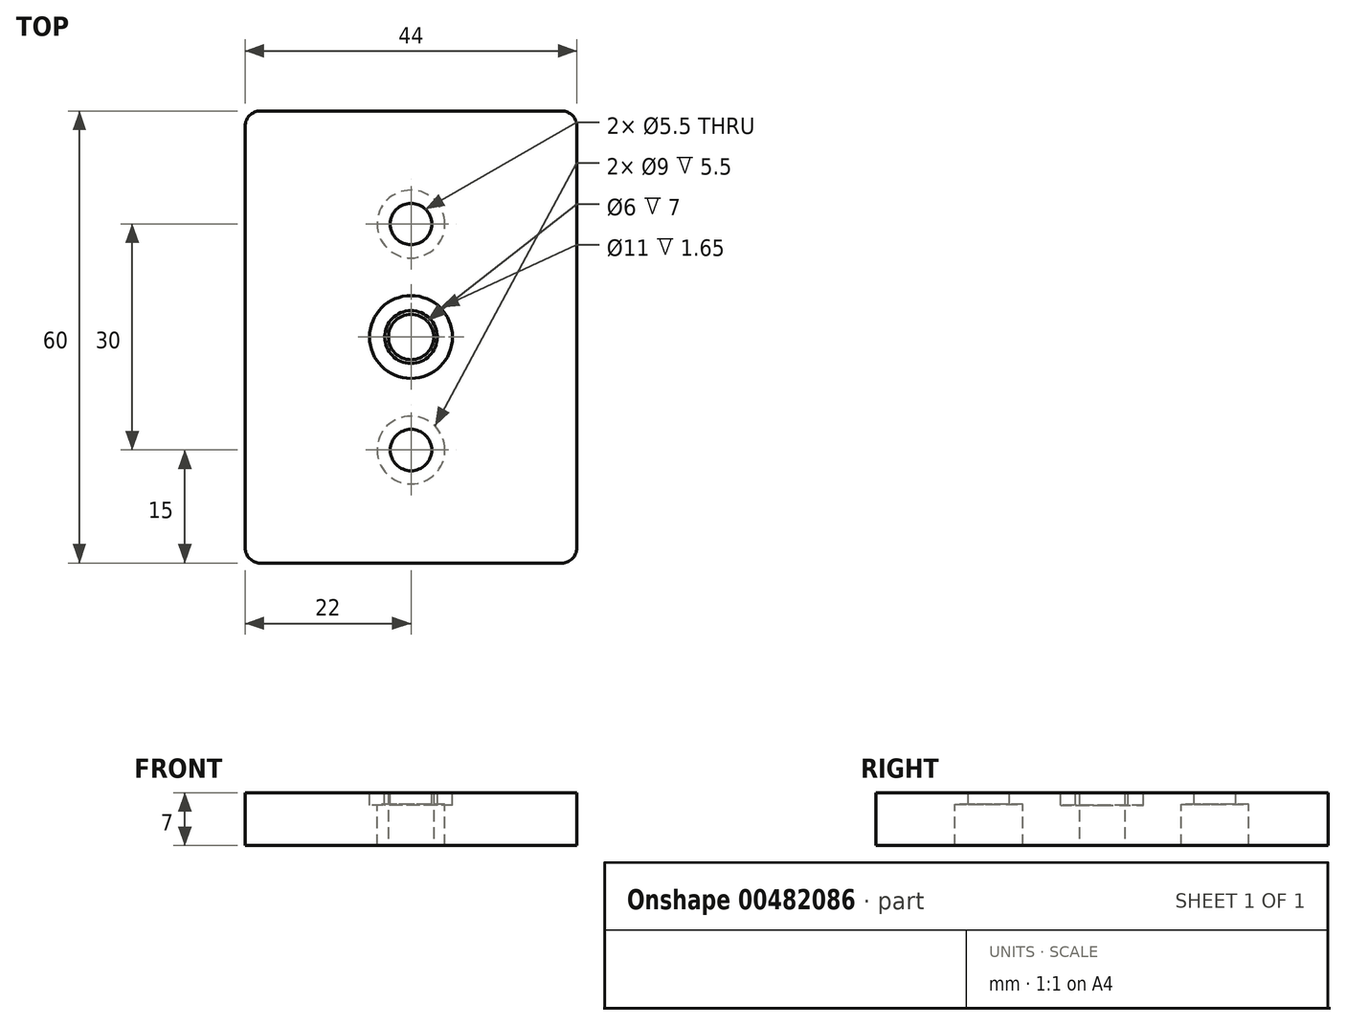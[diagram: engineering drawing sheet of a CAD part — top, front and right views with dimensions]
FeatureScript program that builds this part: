
annotation { "Feature Type Name" : "Feature", "Feature Type Description" : "" }
export const myFeature = defineFeature(function(context is Context, id is Id, definition is map)
    precondition{}
    {
        {
            var Q0;
            Q0=qCreatedBy(makeId("Top.planeOp"),FACE);
            var sketch = newSketch(context, id + "F0", { "sketchPlane" : qUnion([Q0])});
            skLineSegment(sketch, "E0.bottom", {"start": v(-22, 30) * mm, "end": v(22, 30) * mm});
            skLineSegment(sketch, "E0.top", {"start": v(-22, -30) * mm, "end": v(22, -30) * mm});
            skLineSegment(sketch, "E0.left", {"start": v(-22, 30) * mm, "end": v(-22, -30) * mm});
            skLineSegment(sketch, "E0.right", {"start": v(22, 30) * mm, "end": v(22, -30) * mm});
            skSolve(sketch);
        }
        {
            var Q0;
            Q0=makeQuery(id+"F0.imprint","IMPRINT",FACE,{"disambiguationData":[TD([[makeQuery(id+"F0.imprint","IMPRINT",EDGE,{"derivedFrom":sQuery(id+"F0.wireOp",EDGE,"E0.bottom")}),-1.0]])]});
            extrude(context, id + "F1", {"entities" : qUnion([Q0]), "depth" : 7 * mm, "offsetDistance" : 25 * mm});
        }
        {
            var Q0;
            Q0=makeQuery(id+"F1.opExtrude","SWEPT_EDGE",EDGE,{"disambiguationData":[OSD([sQuery(id+"F0.wireOp",EDGE,"E0.top"),sQuery(id+"F0.wireOp",EDGE,"E0.left")])]});
            var Q1;
            Q1=makeQuery(id+"F1.opExtrude","SWEPT_EDGE",EDGE,{"disambiguationData":[OSD([sQuery(id+"F0.wireOp",EDGE,"E0.top"),sQuery(id+"F0.wireOp",EDGE,"E0.right")])]});
            var Q2;
            Q2=makeQuery(id+"F1.opExtrude","SWEPT_EDGE",EDGE,{"disambiguationData":[OSD([sQuery(id+"F0.wireOp",EDGE,"E0.bottom"),sQuery(id+"F0.wireOp",EDGE,"E0.right")])]});
            var Q3;
            Q3=makeQuery(id+"F1.opExtrude","SWEPT_EDGE",EDGE,{"disambiguationData":[OSD([sQuery(id+"F0.wireOp",EDGE,"E0.bottom"),sQuery(id+"F0.wireOp",EDGE,"E0.left")])]});
            fillet(context, id + "F2", {"entities" : qUnion([Q0, Q1, Q2, Q3]), "radius" : 2 * mm, "tangentPropagation" : true, "allowEdgeOverflow" : false});
        }
        {
            var Q0;
            Q0=makeQuery(id+"F1.opExtrude","CAP_FACE",FACE,{"disambiguationData":[OSD([sQuery(id+"F0.wireOp",EDGE,"E0.bottom"),sQuery(id+"F0.wireOp",EDGE,"E0.top"),sQuery(id+"F0.wireOp",EDGE,"E0.left"),sQuery(id+"F0.wireOp",EDGE,"E0.right")])],"isStart":true});
            var sketch = newSketch(context, id + "F3", { "sketchPlane" : qUnion([Q0])});
            skCircle(sketch, "E1", {"center": v(0, 0) * mm, "radius": 3 * mm});
            skPoint(sketch, "E2", {"position": v(0, -15) * mm});
            skPoint(sketch, "E3", {"position": v(0, 15) * mm});
            skSolve(sketch);
        }
        {
            var Q0;
            Q0=makeQuery(id+"F3.imprint","IMPRINT",FACE,{"disambiguationData":[TD([[makeQuery(id+"F3.imprint","IMPRINT",EDGE,{"derivedFrom":sQuery(id+"F3.wireOp",EDGE,"E1")}),1.0]])]});
            extrude(context, id + "F4", {"entities" : qUnion([Q0]), "operationType" : NewBodyOperationType.REMOVE, "endBound" : BoundingType.THROUGH_ALL, "oppositeDirection" : true, "depth" : 25 * mm, "offsetDistance" : 25 * mm});
        }
        {
            var Q0;
            Q0=sQuery(id+"F3.wireOp",VERTEX,"E2");
            var Q1;
            Q1=sQuery(id+"F3.wireOp",VERTEX,"E3");
            var Q2;
            Q2=makeQuery(id+"F1.opExtrude","SWEPT_BODY",BODY,{"disambiguationData":[OSD([sQuery(id+"F0.wireOp",EDGE,"E0.bottom"),sQuery(id+"F0.wireOp",EDGE,"E0.top"),sQuery(id+"F0.wireOp",EDGE,"E0.left"),sQuery(id+"F0.wireOp",EDGE,"E0.right")])]});
            hole(context, id + "F5", {"style" : HoleStyle.C_BORE, "endStyle" : HoleEndStyle.THROUGH, "holeDiameter" : 5.5 * mm, "cBoreDiameter" : 9 * mm, "cBoreDepth" : 5.5 * mm, "isTappedThrough" : true, "tappedDepth" : 5.6 * mm, "tapClearance" : 8, "locations" : qUnion([Q0, Q1]), "scope" : qUnion([Q2]), "startStyle" : HoleStartStyle.SKETCH});
        }
        {
            var Q0;
            Q0=makeQuery(id+"F1.opExtrude","CAP_FACE",FACE,{"disambiguationData":[OSD([sQuery(id+"F0.wireOp",EDGE,"E0.bottom"),sQuery(id+"F0.wireOp",EDGE,"E0.top"),sQuery(id+"F0.wireOp",EDGE,"E0.left"),sQuery(id+"F0.wireOp",EDGE,"E0.right")])],"isStart":false});
            var sketch = newSketch(context, id + "F6", { "sketchPlane" : qUnion([Q0])});
            skCircle(sketch, "E4", {"center": v(0, 0) * mm, "radius": 5.5 * mm});
            skCircle(sketch, "E5", {"center": v(0, 0) * mm, "radius": 3.5 * mm});
            skSolve(sketch);
        }
        {
            var Q0;
            Q0=makeQuery(id+"F6.imprint","IMPRINT",FACE,{"disambiguationData":[TD([[makeQuery(id+"F6.imprint","IMPRINT",EDGE,{"derivedFrom":sQuery(id+"F6.wireOp",EDGE,"E4")}),1.0]])]});
            extrude(context, id + "F7", {"entities" : qUnion([Q0]), "operationType" : NewBodyOperationType.REMOVE, "oppositeDirection" : true, "depth" : 1.65 * mm, "offsetDistance" : 25 * mm});
        }
    });
